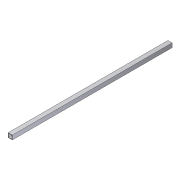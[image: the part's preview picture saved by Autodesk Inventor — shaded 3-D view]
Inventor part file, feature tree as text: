
AUTODESK INVENTOR PART (.ipt)
format: ipt  version: 2012 (Build 160160000, 160)  size: 70,656 bytes
history: native  units: in
note: dims shown in document units (in); Inventor stores cm internally (conversion verified against a paired STEP export)
features: extrude x1, sketch x1
ambient origin geometry x8: Origin, YZ Plane, XZ Plane, XY Plane, X Axis, Y Axis, Z Axis, Center Point
bodies: Solid1 (feature_tree)
feature tree (2):
  extrude  "Extrusion1"  Depth=0.125in
  sketch  "Sketch1"  dims[d0=1.25in d1=0.125in d2=47.75in d3=0.0in]
